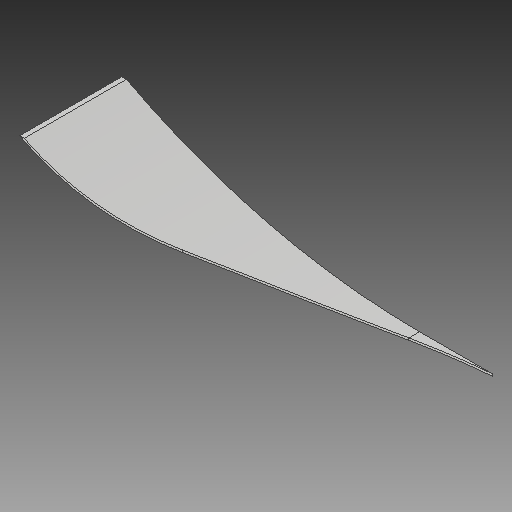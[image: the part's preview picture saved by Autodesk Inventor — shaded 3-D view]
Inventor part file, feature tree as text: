
AUTODESK INVENTOR PART (.ipt)
format: ipt  version: 2018 (Build 220112000, 112)  size: 135,680 bytes
history: native  units: mm
features: other x4, extrude x1, sketch x1, projected_geometry x1
ambient origin geometry x8: Origin, YZ Plane, XZ Plane, XY Plane, X Axis, Y Axis, Z Axis, Center Point
bodies: Body1 (feature_tree)
feature tree (7):
  other  "splitter.ipt"
  extrude  "押し出し1"  Depth=10.0mm
  other  "ソリッド162::splitter.ipt"
  other  "TaggingFeature1"
  sketch  "スケッチ1"
  projected_geometry  "投影ループ1"
  other  "ソリッド1"
